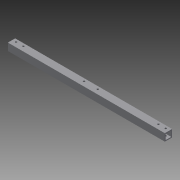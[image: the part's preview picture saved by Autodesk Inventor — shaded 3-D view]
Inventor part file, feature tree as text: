
AUTODESK INVENTOR PART (.ipt)
format: ipt  version: 2015 (Build 190159000, 159)  size: 109,056 bytes
history: native  units: in
note: dims shown in document units (in); Inventor stores cm internally (conversion verified against a paired STEP export)
features: sketch x3, hole x2, projected_geometry x2, extrude x1
ambient origin geometry x8: Origin, YZ Plane, XZ Plane, XY Plane, X Axis, Y Axis, Z Axis, Center Point
bodies: Solid1 (feature_tree)
feature tree (8):
  extrude  "Extrusion1"  Depth=1.0in
  hole  "Hole1"  [1 undecoded]
  hole  "Hole4"  [1 undecoded]
  sketch  "Sketch1"  dims[d0=1.0in d1=1.0in]
  sketch  "Sketch2"  dims[d2=0.75in d3=0.75in]
  projected_geometry  "Projected Loop1"
  sketch  "Sketch3"  dims[d4=0.125in d5=0.125in d6=21.5in d7=0.0in d8=0.625in d9=0.5in d10=0.5in d11=0.625in d12=0.25in d13=0.75in d14=0.375in d15=0.25in d16=0.5635in d17=1.0in d18=0.8108in d19=1.5in d20=1.5in d21=0.625in d22=0.625in d30=0.625in d31=9.8125in d39=9.8125in d40=0.625in d41=0.25in d42=0.75in d43=0.375in d44=0.25in d45=0.5635in d46=1.0in d47=0.8108in]
  projected_geometry  "Projected Loop2"
note: 2 required parameter values undecoded (feature->parameter linkage not recoverable at this tier; creation-order binding heuristic only, values carry confidence <= 0.55)
